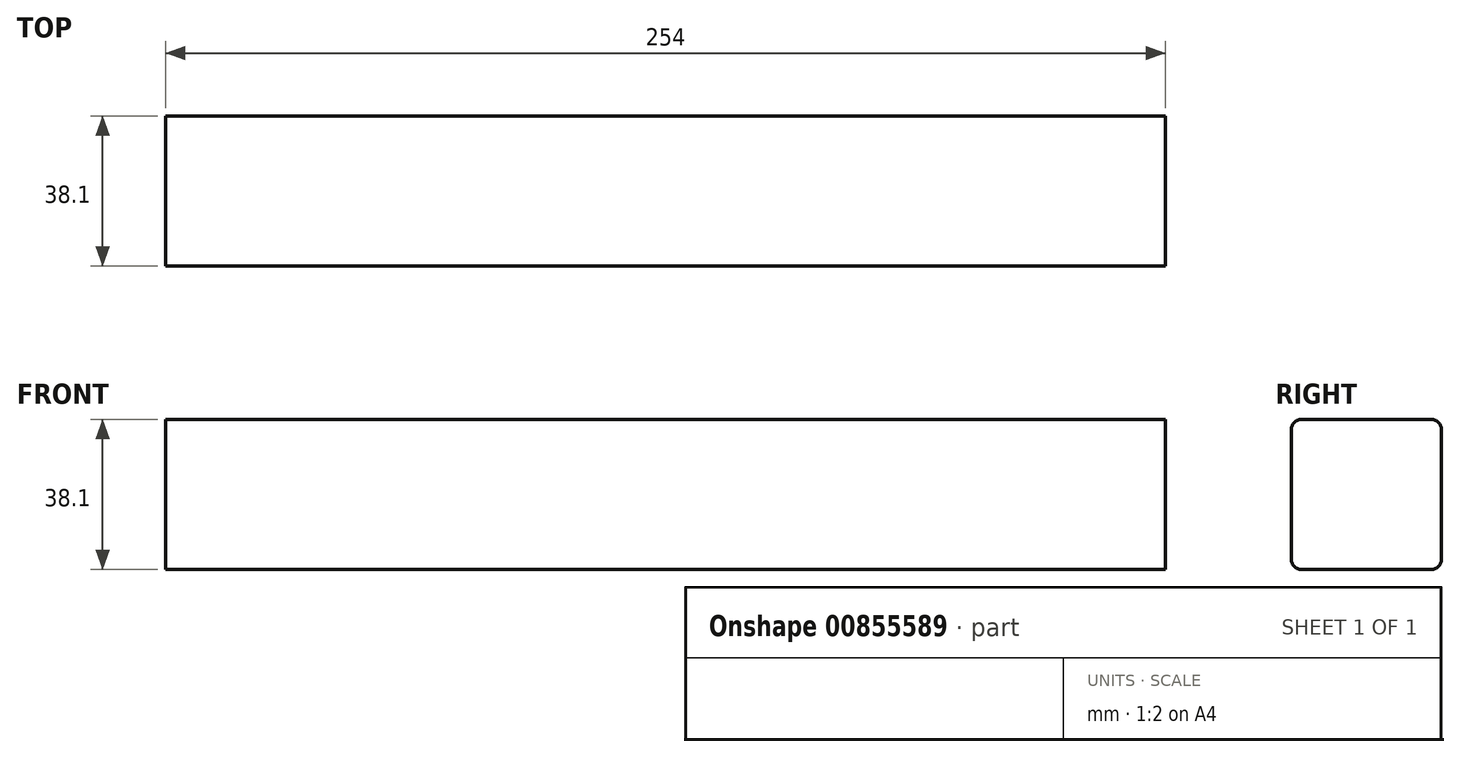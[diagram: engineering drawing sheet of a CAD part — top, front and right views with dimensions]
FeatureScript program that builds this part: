
annotation { "Feature Type Name" : "Feature", "Feature Type Description" : "" }
export const myFeature = defineFeature(function(context is Context, id is Id, definition is map)
    precondition{}
    {
        {
            var Q0;
            Q0=qCreatedBy(makeId("Right.planeOp"),FACE);
            var sketch = newSketch(context, id + "F0", { "sketchPlane" : qUnion([Q0])});
            skLineSegment(sketch, "E0.bottom", {"start": v(2.54, 0) * mm, "end": v(35.56, 0) * mm});
            skLineSegment(sketch, "E0.top", {"start": v(2.54, 38.1) * mm, "end": v(35.56, 38.1) * mm});
            skLineSegment(sketch, "E0.left", {"start": v(0, 2.54) * mm, "end": v(0, 35.56) * mm});
            skLineSegment(sketch, "E0.right", {"start": v(38.1, 2.54) * mm, "end": v(38.1, 35.56) * mm});
            skPoint(sketch, "E1.visualSharp", {"position": v(38.1, 38.1) * mm});
            skArc(sketch, "E1.filletArc", {"start": v(38.1, 35.56) * mm, "mid": v(37.36, 37.36) * mm, "end": v(35.56, 38.1) * mm});
            skPoint(sketch, "E2.visualSharp", {"position": v(0, 38.1) * mm});
            skArc(sketch, "E2.filletArc", {"start": v(2.54, 38.1) * mm, "mid": v(0.74, 37.36) * mm, "end": v(0, 35.56) * mm});
            skPoint(sketch, "E3.visualSharp", {"position": v(0, 0) * mm});
            skArc(sketch, "E3.filletArc", {"start": v(0, 2.54) * mm, "mid": v(0.74, 0.74) * mm, "end": v(2.54, 0) * mm});
            skPoint(sketch, "E4.visualSharp", {"position": v(38.1, 0) * mm});
            skArc(sketch, "E4.filletArc", {"start": v(35.56, 0) * mm, "mid": v(37.36, 0.74) * mm, "end": v(38.1, 2.54) * mm});
            skSolve(sketch);
        }
        {
            var Q0;
            Q0 = qSketchRegion(id + "F0", true);
            extrude(context, id + "F1", {"entities" : qUnion([Q0]), "depth" : 254 * mm, "offsetDistance" : 25.4 * mm});
        }
    });
